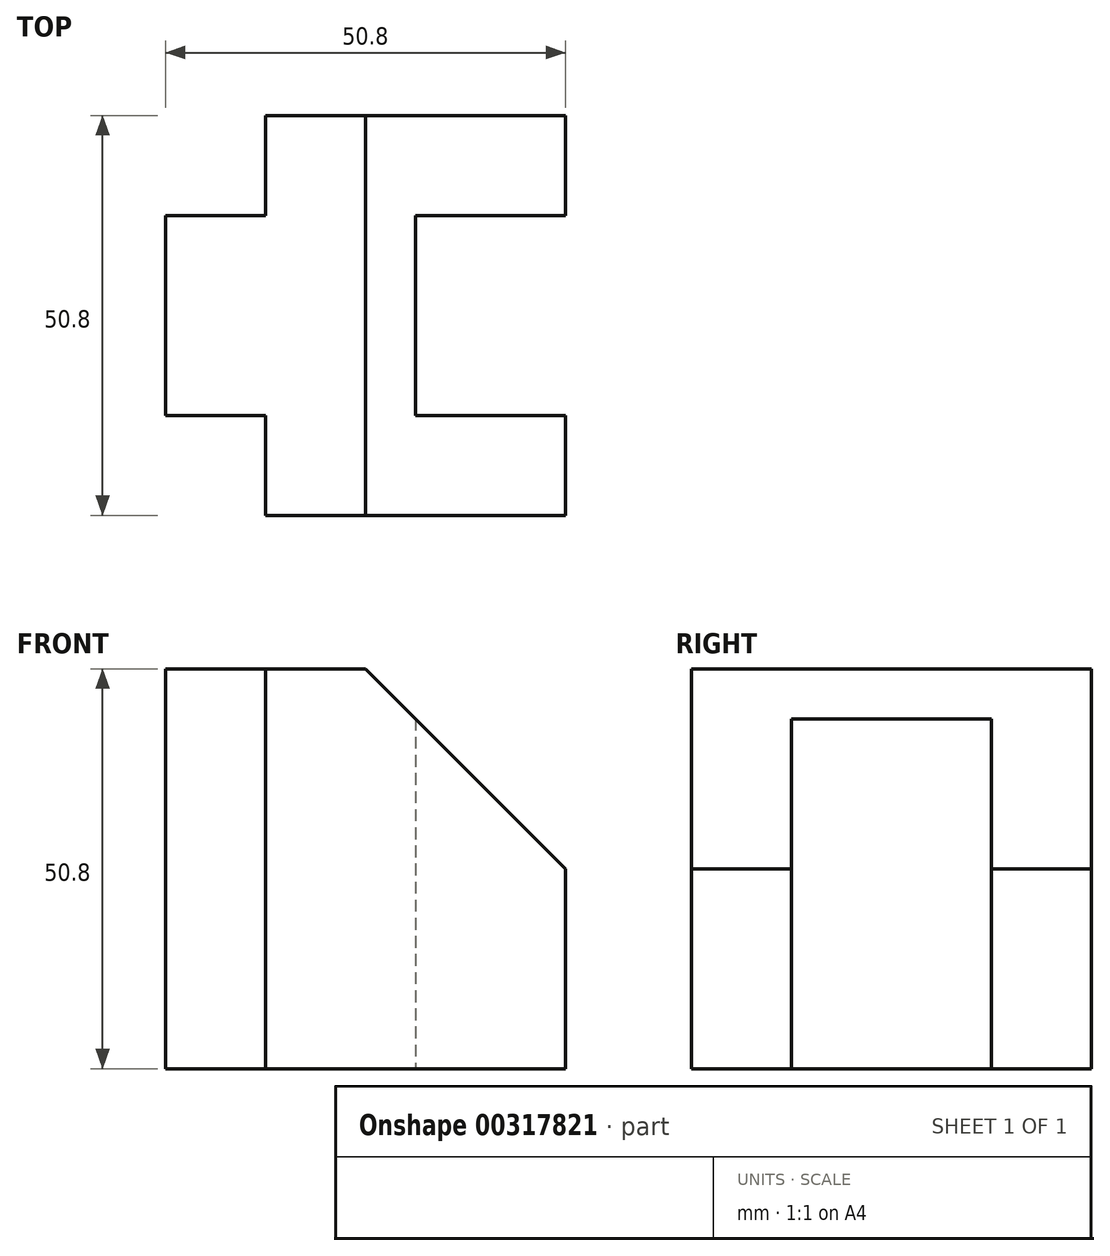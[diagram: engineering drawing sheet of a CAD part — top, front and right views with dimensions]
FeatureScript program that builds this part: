
annotation { "Feature Type Name" : "Feature", "Feature Type Description" : "" }
export const myFeature = defineFeature(function(context is Context, id is Id, definition is map)
    precondition{}
    {
        {
            var Q0;
            Q0=qCreatedBy(makeId("Front.planeOp"),FACE);
            var sketch = newSketch(context, id + "F0", { "sketchPlane" : qUnion([Q0])});
            skLineSegment(sketch, "E0", {"start": v(0, 0) * mm, "end": v(0, 50.8) * mm});
            skLineSegment(sketch, "E1", {"start": v(0, 0) * mm, "end": v(50.8, 0) * mm});
            skLineSegment(sketch, "E2", {"start": v(50.8, 0) * mm, "end": v(50.8, 25.4) * mm});
            skLineSegment(sketch, "E3", {"start": v(0, 50.8) * mm, "end": v(25.4, 50.8) * mm});
            skLineSegment(sketch, "E4", {"start": v(25.4, 50.8) * mm, "end": v(50.8, 25.4) * mm});
            skSolve(sketch);
        }
        {
            var Q0;
            Q0 = qSketchRegion(id + "F0", true);
            extrude(context, id + "F1", {"entities" : qUnion([Q0]), "depth" : 50.8 * mm});
        }
        {
            var Q0;
            Q0=makeQuery(id+"F1.opExtrude","SWEPT_FACE",FACE,{"disambiguationData":[OSD([sQuery(id+"F0.wireOp",EDGE,"E0")])]});
            var sketch = newSketch(context, id + "F2", { "sketchPlane" : qUnion([Q0])});
            skLineSegment(sketch, "E5", {"start": v(12.7, 50.8) * mm, "end": v(12.7, 0) * mm});
            skLineSegment(sketch, "E6", {"start": v(12.7, 0) * mm, "end": v(38.1, 0) * mm});
            skLineSegment(sketch, "E7", {"start": v(38.1, 0) * mm, "end": v(38.1, 50.8) * mm});
            skLineSegment(sketch, "E8", {"start": v(38.1, 50.8) * mm, "end": v(12.7, 50.8) * mm});
            skSolve(sketch);
        }
        {
            var Q0;
            Q0 = qSketchRegion(id + "F2", true);
            extrude(context, id + "F3", {"entities" : qUnion([Q0]), "operationType" : NewBodyOperationType.REMOVE, "endBound" : BoundingType.THROUGH_ALL, "oppositeDirection" : true, "depth" : 50.8 * mm, "hasSecondDirection" : true, "secondDirectionOppositeDirection" : true, "secondDirectionDepth" : 31.75 * mm});
        }
        {
            var Q0;
            Q0=makeQuery(id+"F1.opExtrude","SWEPT_FACE",FACE,{"disambiguationData":[OSD([sQuery(id+"F0.wireOp",EDGE,"E3")])]});
            var sketch = newSketch(context, id + "F4", { "sketchPlane" : qUnion([Q0])});
            skLineSegment(sketch, "E9.bottom", {"start": v(0, -50.8) * mm, "end": v(12.7, -50.8) * mm});
            skLineSegment(sketch, "E9.top", {"start": v(0, -38.1) * mm, "end": v(12.7, -38.1) * mm});
            skLineSegment(sketch, "E9.left", {"start": v(0, -50.8) * mm, "end": v(0, -38.1) * mm});
            skLineSegment(sketch, "E9.right", {"start": v(12.7, -50.8) * mm, "end": v(12.7, -38.1) * mm});
            skLineSegment(sketch, "E10.bottom", {"start": v(0, 0) * mm, "end": v(12.7, 0) * mm});
            skLineSegment(sketch, "E10.top", {"start": v(0, -12.7) * mm, "end": v(12.7, -12.7) * mm});
            skLineSegment(sketch, "E10.left", {"start": v(0, 0) * mm, "end": v(0, -12.7) * mm});
            skLineSegment(sketch, "E10.right", {"start": v(12.7, 0) * mm, "end": v(12.7, -12.7) * mm});
            skSolve(sketch);
        }
        {
            var Q0;
            Q0 = qSketchRegion(id + "F4", true);
            extrude(context, id + "F5", {"entities" : qUnion([Q0]), "operationType" : NewBodyOperationType.REMOVE, "endBound" : BoundingType.THROUGH_ALL, "oppositeDirection" : true, "depth" : 25.4 * mm});
        }
    });
